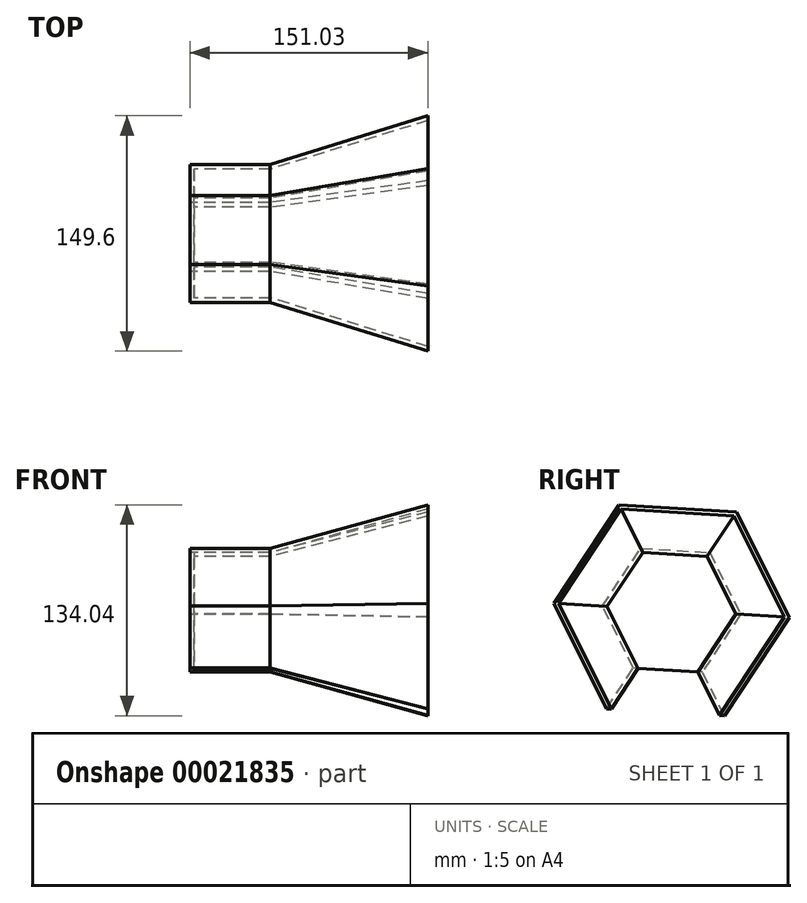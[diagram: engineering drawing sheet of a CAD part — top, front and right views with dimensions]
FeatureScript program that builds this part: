
annotation { "Feature Type Name" : "Feature", "Feature Type Description" : "" }
export const myFeature = defineFeature(function(context is Context, id is Id, definition is map)
    precondition{}
    {
        {
            var Q0;
            Q0=qCreatedBy(makeId("Right.planeOp"),FACE);
            var sketch = newSketch(context, id + "F0", { "sketchPlane" : qUnion([Q0])});
            skCircle(sketch, "E0.cCircle", {"center": v(10.82, 2.63) * mm, "radius": 43.92 * mm, "construction": true});
            skLineSegment(sketch, "E0.0", {"start": v(35.02, 39.28) * mm, "end": v(54.66, 0) * mm});
            skLineSegment(sketch, "E0.1", {"start": v(54.66, 0) * mm, "end": v(30.46, -36.65) * mm});
            skLineSegment(sketch, "E0.2", {"start": v(30.46, -36.65) * mm, "end": v(-13.38, -34.02) * mm});
            skLineSegment(sketch, "E0.3", {"start": v(-13.38, -34.02) * mm, "end": v(-33.02, 5.27) * mm});
            skLineSegment(sketch, "E0.4", {"start": v(-33.02, 5.27) * mm, "end": v(-8.82, 41.92) * mm});
            skLineSegment(sketch, "E0.5", {"start": v(-8.82, 41.92) * mm, "end": v(35.02, 39.28) * mm});
            skLineSegment(sketch, "E1", {"start": v(66.76, 18.33) * mm, "end": v(35.02, 39.28) * mm});
            skSolve(sketch);
        }
        {
            var Q0;
            Q0 = qSketchRegion(id + "F0", true);
            extrude(context, id + "F1", {"entities" : qUnion([Q0]), "depth" : 100.23 * mm, "hasDraft" : true, "draftAngle" : 15 * degree, "hasSecondDirection" : true, "secondDirectionOppositeDirection" : true, "secondDirectionDepth" : 50.8 * mm});
        }
        {
            var Q0;
            Q0=makeQuery(id+"F1.opExtrude","SWEPT_FACE",FACE,{"disambiguationData":[OSD([sQuery(id+"F0.wireOp",EDGE,"E0.2")])]});
            var Q1;
            Q1=makeQuery(id+"F1.opExtrude","CAP_FACE",FACE,{"disambiguationData":[OSD([sQuery(id+"F0.wireOp",EDGE,"E0.0"),sQuery(id+"F0.wireOp",EDGE,"E0.1"),sQuery(id+"F0.wireOp",EDGE,"E0.2"),sQuery(id+"F0.wireOp",EDGE,"E0.3"),sQuery(id+"F0.wireOp",EDGE,"E0.4"),sQuery(id+"F0.wireOp",EDGE,"E0.5")])],"isStart":false});
            shell(context, id + "F2", {"entities" : qUnion([Q0, Q1]), "thickness" : 2.54 * mm});
        }
    });
